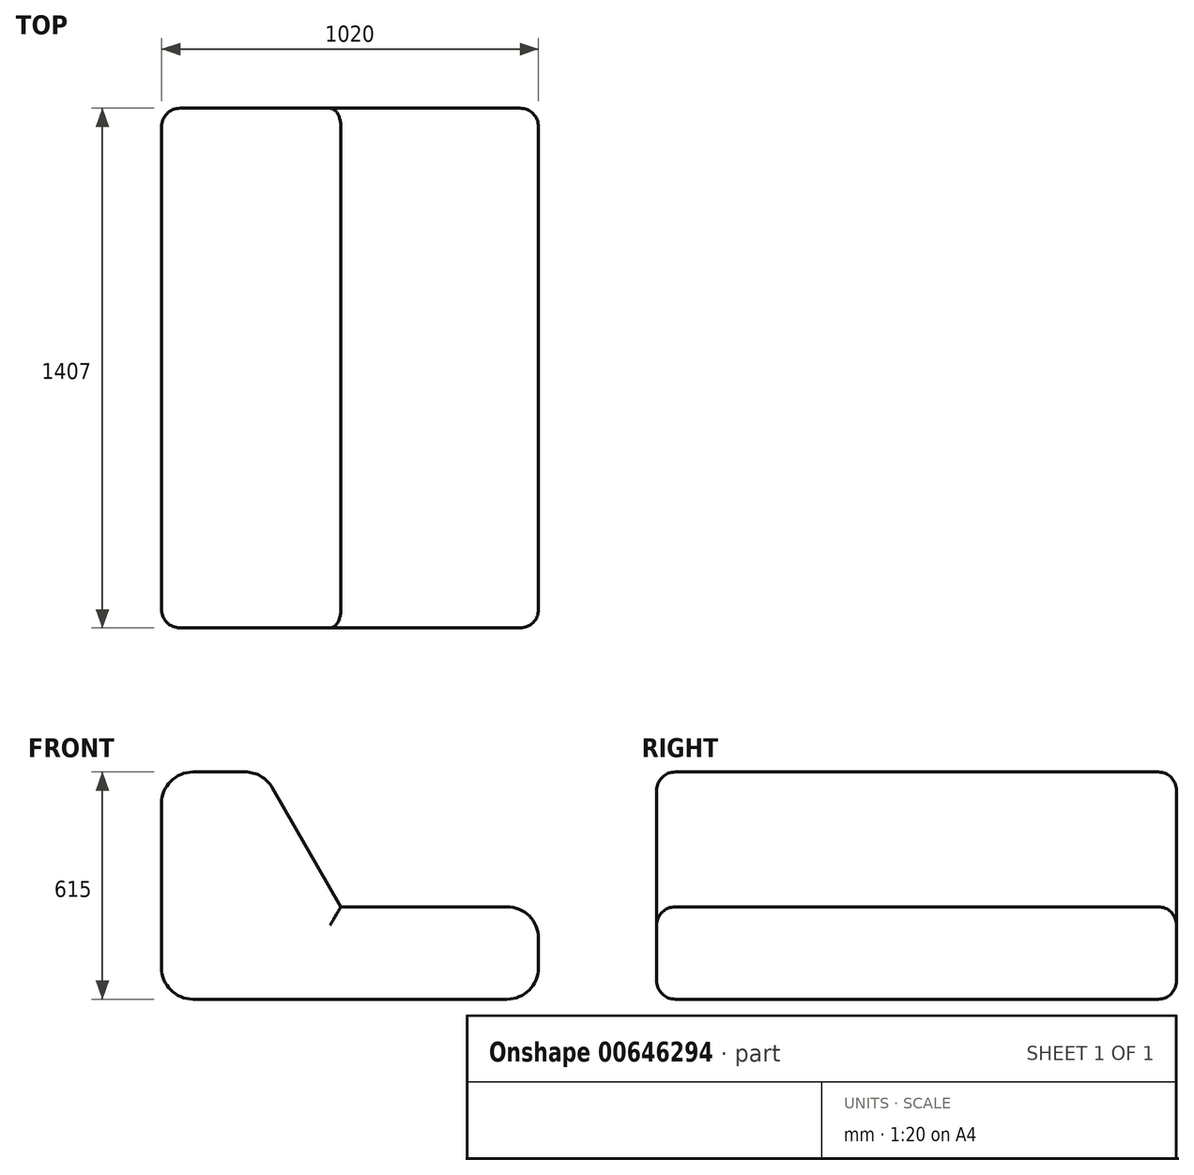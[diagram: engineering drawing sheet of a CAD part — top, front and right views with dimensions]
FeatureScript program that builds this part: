
annotation { "Feature Type Name" : "Feature", "Feature Type Description" : "" }
export const myFeature = defineFeature(function(context is Context, id is Id, definition is map)
    precondition{}
    {
        {
            var Q0;
            Q0=qCreatedBy(makeId("Front.planeOp"),FACE);
            var sketch = newSketch(context, id + "F0", { "sketchPlane" : qUnion([Q0])});
            skLineSegment(sketch, "E0", {"start": v(0, 0) * mm, "end": v(0, 615) * mm});
            skLineSegment(sketch, "E1", {"start": v(0, 615) * mm, "end": v(275, 615) * mm});
            skLineSegment(sketch, "E2", {"start": v(275, 615) * mm, "end": v(485, 250) * mm});
            skLineSegment(sketch, "E3", {"start": v(485, 250) * mm, "end": v(1020, 250) * mm});
            skLineSegment(sketch, "E4", {"start": v(1020, 250) * mm, "end": v(1020, 0) * mm});
            skLineSegment(sketch, "E5", {"start": v(1020, 0) * mm, "end": v(0, 0) * mm});
            skSolve(sketch);
        }
        {
            var Q0;
            Q0 = qSketchRegion(id + "F0", true);
            extrude(context, id + "F1", {"entities" : qUnion([Q0]), "depth" : 1407 * mm, "offsetDistance" : 25 * mm});
        }
        {
            var Q0;
            Q0=makeQuery(id+"F1.opExtrude","SWEPT_EDGE",EDGE,{"disambiguationData":[OSD([sQuery(id+"F0.wireOp",EDGE,"E1"),sQuery(id+"F0.wireOp",EDGE,"E2")])]});
            var Q1;
            Q1=makeQuery(id+"F1.opExtrude","SWEPT_EDGE",EDGE,{"disambiguationData":[OSD([sQuery(id+"F0.wireOp",EDGE,"E3"),sQuery(id+"F0.wireOp",EDGE,"E4")])]});
            var Q2;
            Q2=makeQuery(id+"F1.opExtrude","SWEPT_EDGE",EDGE,{"disambiguationData":[OSD([sQuery(id+"F0.wireOp",EDGE,"E4"),sQuery(id+"F0.wireOp",EDGE,"E5")])]});
            var Q3;
            Q3=makeQuery(id+"F1.opExtrude","SWEPT_EDGE",EDGE,{"disambiguationData":[OSD([sQuery(id+"F0.wireOp",EDGE,"E0"),sQuery(id+"F0.wireOp",EDGE,"E5")])]});
            var Q4;
            Q4=makeQuery(id+"F1.opExtrude","SWEPT_EDGE",EDGE,{"disambiguationData":[OSD([sQuery(id+"F0.wireOp",EDGE,"E0"),sQuery(id+"F0.wireOp",EDGE,"E1")])]});
            fillet(context, id + "F2", {"entities" : qUnion([Q0, Q1, Q2, Q3, Q4]), "radius" : 85 * mm, "tangentPropagation" : true, "allowEdgeOverflow" : false});
        }
        {
            var Q0;
            Q0=makeQuery(id+"F1.opExtrude","CAP_EDGE",EDGE,{"disambiguationData":[OSD([sQuery(id+"F0.wireOp",EDGE,"E2")])],"isStart":true});
            var Q1;
            Q1=makeQuery(id+"F1.opExtrude","CAP_EDGE",EDGE,{"disambiguationData":[OSD([sQuery(id+"F0.wireOp",EDGE,"E1")])],"isStart":true});
            var Q2;
            {var subQ0=sQuery(id+"F0.wireOp",EDGE,"E2");var subQ1=sQuery(id+"F0.wireOp",EDGE,"E1");Q2=makeQuery(id+"F2.opFillet","BLEND_EDGE",EDGE,{"blendedFrom":[makeQuery(id+"F1.opExtrude","SWEPT_EDGE",EDGE,{"disambiguationData":[OSD([subQ1,subQ0])]}),makeQuery(id+"F1.opExtrude","CAP_FACE",FACE,{"disambiguationData":[OSD([sQuery(id+"F0.wireOp",EDGE,"E0"),subQ1,subQ0,sQuery(id+"F0.wireOp",EDGE,"E3"),sQuery(id+"F0.wireOp",EDGE,"E4"),sQuery(id+"F0.wireOp",EDGE,"E5")])],"isStart":true})],"blendedInto":[makeQuery(id+"F1.opExtrude","CAP_FACE",FACE,{"disambiguationData":[OSD([sQuery(id+"F0.wireOp",EDGE,"E0"),subQ1,subQ0,sQuery(id+"F0.wireOp",EDGE,"E3"),sQuery(id+"F0.wireOp",EDGE,"E4"),sQuery(id+"F0.wireOp",EDGE,"E5")])],"isStart":true})]});}
            var Q3;
            Q3=makeQuery(id+"F1.opExtrude","CAP_EDGE",EDGE,{"disambiguationData":[OSD([sQuery(id+"F0.wireOp",EDGE,"E3")])],"isStart":true});
            var Q4;
            {var subQ0=sQuery(id+"F0.wireOp",EDGE,"E4");var subQ1=sQuery(id+"F0.wireOp",EDGE,"E3");Q4=makeQuery(id+"F2.opFillet","BLEND_EDGE",EDGE,{"blendedFrom":[makeQuery(id+"F1.opExtrude","SWEPT_EDGE",EDGE,{"disambiguationData":[OSD([subQ1,subQ0])]}),makeQuery(id+"F1.opExtrude","CAP_FACE",FACE,{"disambiguationData":[OSD([sQuery(id+"F0.wireOp",EDGE,"E0"),sQuery(id+"F0.wireOp",EDGE,"E1"),sQuery(id+"F0.wireOp",EDGE,"E2"),subQ1,subQ0,sQuery(id+"F0.wireOp",EDGE,"E5")])],"isStart":true})],"blendedInto":[makeQuery(id+"F1.opExtrude","CAP_FACE",FACE,{"disambiguationData":[OSD([sQuery(id+"F0.wireOp",EDGE,"E0"),sQuery(id+"F0.wireOp",EDGE,"E1"),sQuery(id+"F0.wireOp",EDGE,"E2"),subQ1,subQ0,sQuery(id+"F0.wireOp",EDGE,"E5")])],"isStart":true})]});}
            var Q5;
            Q5=makeQuery(id+"F1.opExtrude","CAP_EDGE",EDGE,{"disambiguationData":[OSD([sQuery(id+"F0.wireOp",EDGE,"E4")])],"isStart":true});
            var Q6;
            {var subQ0=sQuery(id+"F0.wireOp",EDGE,"E5");var subQ1=sQuery(id+"F0.wireOp",EDGE,"E4");Q6=makeQuery(id+"F2.opFillet","BLEND_EDGE",EDGE,{"blendedFrom":[makeQuery(id+"F1.opExtrude","SWEPT_EDGE",EDGE,{"disambiguationData":[OSD([subQ1,subQ0])]}),makeQuery(id+"F1.opExtrude","CAP_FACE",FACE,{"disambiguationData":[OSD([sQuery(id+"F0.wireOp",EDGE,"E0"),sQuery(id+"F0.wireOp",EDGE,"E1"),sQuery(id+"F0.wireOp",EDGE,"E2"),sQuery(id+"F0.wireOp",EDGE,"E3"),subQ1,subQ0])],"isStart":true})],"blendedInto":[makeQuery(id+"F1.opExtrude","CAP_FACE",FACE,{"disambiguationData":[OSD([sQuery(id+"F0.wireOp",EDGE,"E0"),sQuery(id+"F0.wireOp",EDGE,"E1"),sQuery(id+"F0.wireOp",EDGE,"E2"),sQuery(id+"F0.wireOp",EDGE,"E3"),subQ1,subQ0])],"isStart":true})]});}
            var Q7;
            {var subQ0=sQuery(id+"F0.wireOp",EDGE,"E1");var subQ1=sQuery(id+"F0.wireOp",EDGE,"E0");Q7=makeQuery(id+"F2.opFillet","BLEND_EDGE",EDGE,{"blendedFrom":[makeQuery(id+"F1.opExtrude","SWEPT_EDGE",EDGE,{"disambiguationData":[OSD([subQ1,subQ0])]}),makeQuery(id+"F1.opExtrude","CAP_FACE",FACE,{"disambiguationData":[OSD([subQ1,subQ0,sQuery(id+"F0.wireOp",EDGE,"E2"),sQuery(id+"F0.wireOp",EDGE,"E3"),sQuery(id+"F0.wireOp",EDGE,"E4"),sQuery(id+"F0.wireOp",EDGE,"E5")])],"isStart":true})],"blendedInto":[makeQuery(id+"F1.opExtrude","CAP_FACE",FACE,{"disambiguationData":[OSD([subQ1,subQ0,sQuery(id+"F0.wireOp",EDGE,"E2"),sQuery(id+"F0.wireOp",EDGE,"E3"),sQuery(id+"F0.wireOp",EDGE,"E4"),sQuery(id+"F0.wireOp",EDGE,"E5")])],"isStart":true})]});}
            var Q8;
            Q8=makeQuery(id+"F1.opExtrude","CAP_EDGE",EDGE,{"disambiguationData":[OSD([sQuery(id+"F0.wireOp",EDGE,"E0")])],"isStart":true});
            var Q9;
            {var subQ0=sQuery(id+"F0.wireOp",EDGE,"E5");var subQ1=sQuery(id+"F0.wireOp",EDGE,"E0");Q9=makeQuery(id+"F2.opFillet","BLEND_EDGE",EDGE,{"blendedFrom":[makeQuery(id+"F1.opExtrude","SWEPT_EDGE",EDGE,{"disambiguationData":[OSD([subQ1,subQ0])]}),makeQuery(id+"F1.opExtrude","CAP_FACE",FACE,{"disambiguationData":[OSD([subQ1,sQuery(id+"F0.wireOp",EDGE,"E1"),sQuery(id+"F0.wireOp",EDGE,"E2"),sQuery(id+"F0.wireOp",EDGE,"E3"),sQuery(id+"F0.wireOp",EDGE,"E4"),subQ0])],"isStart":true})],"blendedInto":[makeQuery(id+"F1.opExtrude","CAP_FACE",FACE,{"disambiguationData":[OSD([subQ1,sQuery(id+"F0.wireOp",EDGE,"E1"),sQuery(id+"F0.wireOp",EDGE,"E2"),sQuery(id+"F0.wireOp",EDGE,"E3"),sQuery(id+"F0.wireOp",EDGE,"E4"),subQ0])],"isStart":true})]});}
            var Q10;
            Q10=makeQuery(id+"F1.opExtrude","CAP_EDGE",EDGE,{"disambiguationData":[OSD([sQuery(id+"F0.wireOp",EDGE,"E5")])],"isStart":true});
            var Q11;
            Q11=makeQuery(id+"F1.opExtrude","CAP_EDGE",EDGE,{"disambiguationData":[OSD([sQuery(id+"F0.wireOp",EDGE,"E3")])],"isStart":false});
            var Q12;
            Q12=makeQuery(id+"F1.opExtrude","CAP_EDGE",EDGE,{"disambiguationData":[OSD([sQuery(id+"F0.wireOp",EDGE,"E2")])],"isStart":false});
            var Q13;
            {var subQ0=sQuery(id+"F0.wireOp",EDGE,"E2");var subQ1=sQuery(id+"F0.wireOp",EDGE,"E1");Q13=makeQuery(id+"F2.opFillet","BLEND_EDGE",EDGE,{"blendedFrom":[makeQuery(id+"F1.opExtrude","SWEPT_EDGE",EDGE,{"disambiguationData":[OSD([subQ1,subQ0])]}),makeQuery(id+"F1.opExtrude","CAP_FACE",FACE,{"disambiguationData":[OSD([sQuery(id+"F0.wireOp",EDGE,"E0"),subQ1,subQ0,sQuery(id+"F0.wireOp",EDGE,"E3"),sQuery(id+"F0.wireOp",EDGE,"E4"),sQuery(id+"F0.wireOp",EDGE,"E5")])],"isStart":false})],"blendedInto":[makeQuery(id+"F1.opExtrude","CAP_FACE",FACE,{"disambiguationData":[OSD([sQuery(id+"F0.wireOp",EDGE,"E0"),subQ1,subQ0,sQuery(id+"F0.wireOp",EDGE,"E3"),sQuery(id+"F0.wireOp",EDGE,"E4"),sQuery(id+"F0.wireOp",EDGE,"E5")])],"isStart":false})]});}
            var Q14;
            Q14=makeQuery(id+"F1.opExtrude","CAP_EDGE",EDGE,{"disambiguationData":[OSD([sQuery(id+"F0.wireOp",EDGE,"E1")])],"isStart":false});
            var Q15;
            {var subQ0=sQuery(id+"F0.wireOp",EDGE,"E1");var subQ1=sQuery(id+"F0.wireOp",EDGE,"E0");Q15=makeQuery(id+"F2.opFillet","BLEND_EDGE",EDGE,{"blendedFrom":[makeQuery(id+"F1.opExtrude","SWEPT_EDGE",EDGE,{"disambiguationData":[OSD([subQ1,subQ0])]}),makeQuery(id+"F1.opExtrude","CAP_FACE",FACE,{"disambiguationData":[OSD([subQ1,subQ0,sQuery(id+"F0.wireOp",EDGE,"E2"),sQuery(id+"F0.wireOp",EDGE,"E3"),sQuery(id+"F0.wireOp",EDGE,"E4"),sQuery(id+"F0.wireOp",EDGE,"E5")])],"isStart":false})],"blendedInto":[makeQuery(id+"F1.opExtrude","CAP_FACE",FACE,{"disambiguationData":[OSD([subQ1,subQ0,sQuery(id+"F0.wireOp",EDGE,"E2"),sQuery(id+"F0.wireOp",EDGE,"E3"),sQuery(id+"F0.wireOp",EDGE,"E4"),sQuery(id+"F0.wireOp",EDGE,"E5")])],"isStart":false})]});}
            var Q16;
            Q16=makeQuery(id+"F1.opExtrude","CAP_EDGE",EDGE,{"disambiguationData":[OSD([sQuery(id+"F0.wireOp",EDGE,"E0")])],"isStart":false});
            var Q17;
            {var subQ0=sQuery(id+"F0.wireOp",EDGE,"E5");var subQ1=sQuery(id+"F0.wireOp",EDGE,"E0");Q17=makeQuery(id+"F2.opFillet","BLEND_EDGE",EDGE,{"blendedFrom":[makeQuery(id+"F1.opExtrude","SWEPT_EDGE",EDGE,{"disambiguationData":[OSD([subQ1,subQ0])]}),makeQuery(id+"F1.opExtrude","CAP_FACE",FACE,{"disambiguationData":[OSD([subQ1,sQuery(id+"F0.wireOp",EDGE,"E1"),sQuery(id+"F0.wireOp",EDGE,"E2"),sQuery(id+"F0.wireOp",EDGE,"E3"),sQuery(id+"F0.wireOp",EDGE,"E4"),subQ0])],"isStart":false})],"blendedInto":[makeQuery(id+"F1.opExtrude","CAP_FACE",FACE,{"disambiguationData":[OSD([subQ1,sQuery(id+"F0.wireOp",EDGE,"E1"),sQuery(id+"F0.wireOp",EDGE,"E2"),sQuery(id+"F0.wireOp",EDGE,"E3"),sQuery(id+"F0.wireOp",EDGE,"E4"),subQ0])],"isStart":false})]});}
            var Q18;
            Q18=makeQuery(id+"F1.opExtrude","CAP_EDGE",EDGE,{"disambiguationData":[OSD([sQuery(id+"F0.wireOp",EDGE,"E5")])],"isStart":false});
            var Q19;
            {var subQ0=sQuery(id+"F0.wireOp",EDGE,"E5");var subQ1=sQuery(id+"F0.wireOp",EDGE,"E4");Q19=makeQuery(id+"F2.opFillet","BLEND_EDGE",EDGE,{"blendedFrom":[makeQuery(id+"F1.opExtrude","SWEPT_EDGE",EDGE,{"disambiguationData":[OSD([subQ1,subQ0])]}),makeQuery(id+"F1.opExtrude","CAP_FACE",FACE,{"disambiguationData":[OSD([sQuery(id+"F0.wireOp",EDGE,"E0"),sQuery(id+"F0.wireOp",EDGE,"E1"),sQuery(id+"F0.wireOp",EDGE,"E2"),sQuery(id+"F0.wireOp",EDGE,"E3"),subQ1,subQ0])],"isStart":false})],"blendedInto":[makeQuery(id+"F1.opExtrude","CAP_FACE",FACE,{"disambiguationData":[OSD([sQuery(id+"F0.wireOp",EDGE,"E0"),sQuery(id+"F0.wireOp",EDGE,"E1"),sQuery(id+"F0.wireOp",EDGE,"E2"),sQuery(id+"F0.wireOp",EDGE,"E3"),subQ1,subQ0])],"isStart":false})]});}
            var Q20;
            Q20=makeQuery(id+"F1.opExtrude","CAP_EDGE",EDGE,{"disambiguationData":[OSD([sQuery(id+"F0.wireOp",EDGE,"E4")])],"isStart":false});
            var Q21;
            {var subQ0=sQuery(id+"F0.wireOp",EDGE,"E4");var subQ1=sQuery(id+"F0.wireOp",EDGE,"E3");Q21=makeQuery(id+"F2.opFillet","BLEND_EDGE",EDGE,{"blendedFrom":[makeQuery(id+"F1.opExtrude","SWEPT_EDGE",EDGE,{"disambiguationData":[OSD([subQ1,subQ0])]}),makeQuery(id+"F1.opExtrude","CAP_FACE",FACE,{"disambiguationData":[OSD([sQuery(id+"F0.wireOp",EDGE,"E0"),sQuery(id+"F0.wireOp",EDGE,"E1"),sQuery(id+"F0.wireOp",EDGE,"E2"),subQ1,subQ0,sQuery(id+"F0.wireOp",EDGE,"E5")])],"isStart":false})],"blendedInto":[makeQuery(id+"F1.opExtrude","CAP_FACE",FACE,{"disambiguationData":[OSD([sQuery(id+"F0.wireOp",EDGE,"E0"),sQuery(id+"F0.wireOp",EDGE,"E1"),sQuery(id+"F0.wireOp",EDGE,"E2"),subQ1,subQ0,sQuery(id+"F0.wireOp",EDGE,"E5")])],"isStart":false})]});}
            fillet(context, id + "F3", {"entities" : qUnion([Q0, Q1, Q2, Q3, Q4, Q5, Q6, Q7, Q8, Q9, Q10, Q11, Q12, Q13, Q14, Q15, Q16, Q17, Q18, Q19, Q20, Q21]), "radius" : 50 * mm, "tangentPropagation" : true, "allowEdgeOverflow" : false});
        }
    });
